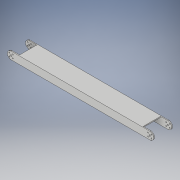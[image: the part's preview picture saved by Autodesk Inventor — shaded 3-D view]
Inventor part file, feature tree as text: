
AUTODESK INVENTOR PART (.ipt)
format: ipt  version: 2017 (Build 210142000, 142)  size: 187,392 bytes
history: native  units: in
note: dims shown in document units (in); Inventor stores cm internally (conversion verified against a paired STEP export)
features: sketch x4, extrude x3, projected_geometry x2, hole x1, fillet x1
ambient origin geometry x8: Origin, YZ Plane, XZ Plane, XY Plane, X Axis, Y Axis, Z Axis, Center Point
bodies: Solid1 (feature_tree)
feature tree (11):
  extrude  "Extrusion1"  Depth=2.2935in
  extrude  "Extrusion2"  Depth=0.125in
  extrude  "Extrusion3"  Depth=2.5435in
  hole  "Hole1"  [1 undecoded]
  fillet  "Fillet1"  Radius=0.1875in
  sketch  "Sketch1"  dims[d0=1.0in d2=2.2935in]
  sketch  "Sketch3"  dims[d3=0.875in d4=0.125in]
  projected_geometry  "Projected Loop2"
  sketch  "Sketch4"  dims[d5=19.5in d6=0.0in d14=2.5435in]
  projected_geometry  "Projected Loop3"
  sketch  "Sketch5"  dims[d16=1.5in d17=0.125in d18=0.0in d19=0.1875in d20=0.5in d21=1.0in d22=0.5in d23=0.1875in d24=0.5in d25=5.0in d26=0.0in d27=1.5in d28=2.2935in d29=0.125in d30=2.2935in d31=0.125in d32=0.125in d33=0.445in d34=0.445in d35=0.2775in d36=0.2775in d37=0.445in d38=0.445in d39=0.2775in d40=0.2775in d43=1.0in d47=0.445in d48=0.445in d49=0.2775in d50=0.2775in d51=0.445in d52=0.445in d53=0.2775in d54=0.2775in d55=0.1378in d56=0.75in d57=0.375in d58=0.25in d59=0.5635in d60=5.0in d61=0.8108in d62=0.5in]
note: 1 required parameter value undecoded (feature->parameter linkage not recoverable at this tier; creation-order binding heuristic only, values carry confidence <= 0.55)
